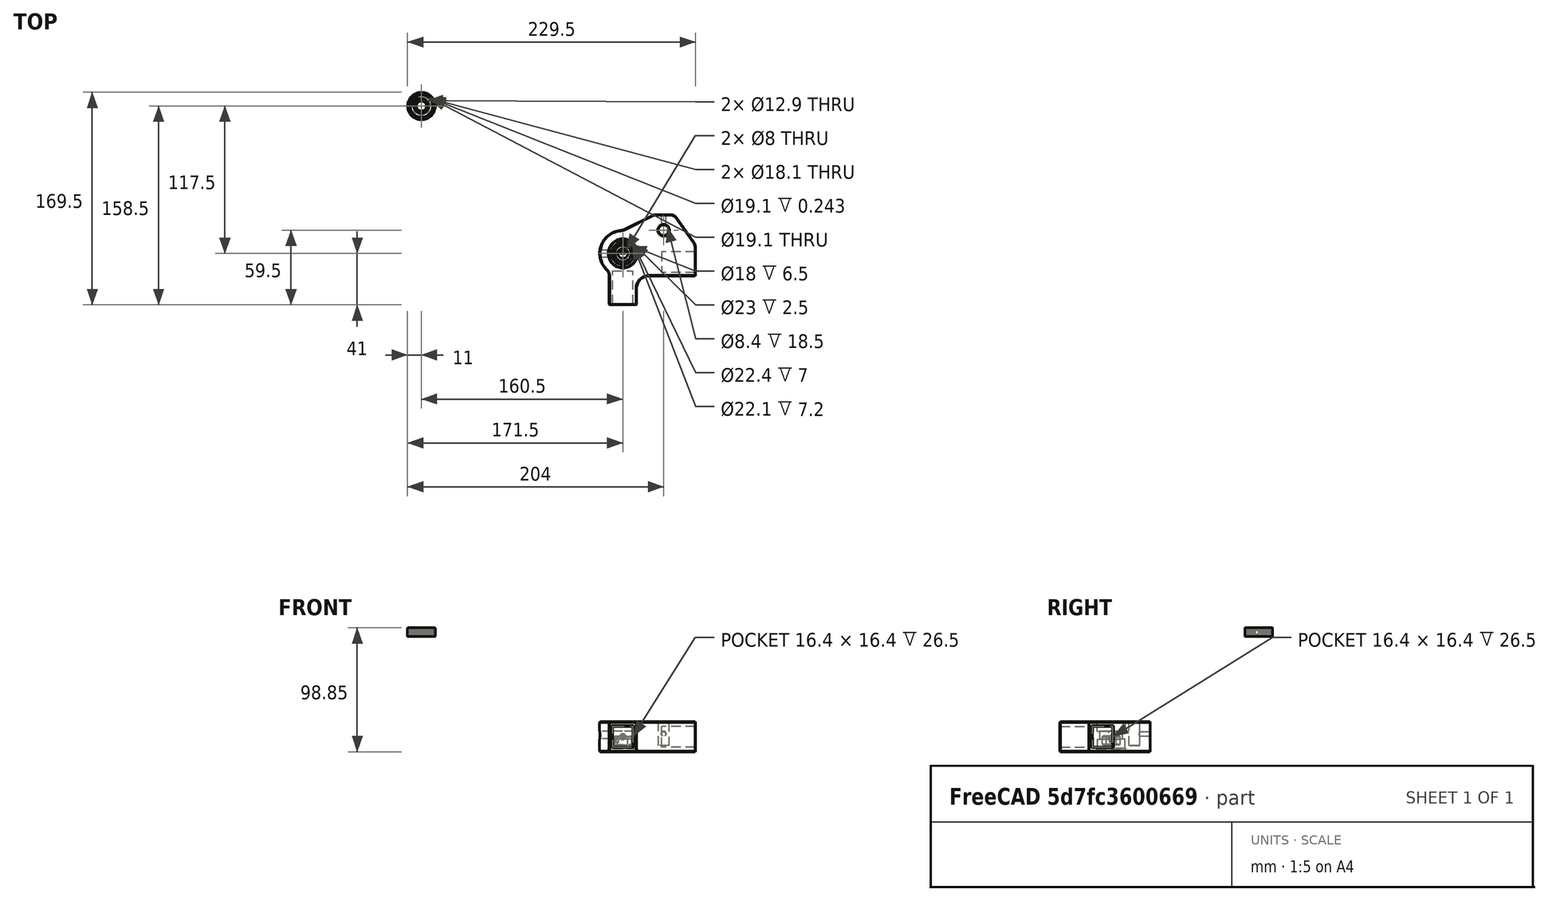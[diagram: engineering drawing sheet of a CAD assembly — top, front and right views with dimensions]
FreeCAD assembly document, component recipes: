
FREECAD ASSEMBLY — COMPONENT RECIPES ("MotorizedBed")

This assembly document has 4 components, labeled P0..P3 below (a component is one placed body or linked part). 1 of them carries a construction recipe — the FreeCAD feature program that regenerates the part from scratch, quoted from this document or its linked companion documents; the rest are supplied as boundary geometry only. No exploded tour is included for this assembly.
COMPONENT P0 — geometry summary ("VerrouillageVisTrapézoidale"; no construction recipe available for this part):
  bounding box: 14.2 x 14.0 x 7.0 mm
  tessellated surface: 100 triangles
  volume: 714 mm^3 (51% of its bounding box)
  symmetry: mirror-symmetric across its z mid-plane
COMPONENT P1 — recipe-attached ("LowerBracketTL", modeled in this document).
Construction recipe (the document's own serialized feature program — sketch geometry with constraints, then the solid features built on it; lengths are millimeters unless a unit is written):

FEATURE [Sketcher::SketchObject] Sketch
  ArcFitTolerance = 1e-06
  FullyConstrained = true
  MapMode = 5
  TreeRank = 141
  sketch-geometry (10):
    g0: LineSegment StartX=-11 StartY=-14.8745 StartZ=0 EndX=-11 EndY=-41 EndZ=0
    g1: LineSegment StartX=-11 StartY=-41 StartZ=0 EndX=11 EndY=-41 EndZ=0
    g2: LineSegment StartX=11 StartY=-41 StartZ=0 EndX=11 EndY=-18 EndZ=0
    g3: LineSegment StartX=11 StartY=-18 StartZ=0 EndX=58 EndY=-18 EndZ=0
    g4: LineSegment StartX=58 StartY=-18 StartZ=0 EndX=58 EndY=7 EndZ=0
    g5: LineSegment StartX=58 StartY=7 StartZ=0 EndX=41 EndY=31 EndZ=0
    g6: LineSegment StartX=41 StartY=31 StartZ=0 EndX=25 EndY=31 EndZ=0
    g7: Circle [constr] CenterX=0 CenterY=0 CenterZ=0 NormalX=0 NormalY=0 NormalZ=1 AngleXU=0 Radius=18.5
    g8: ArcOfCircle CenterX=0 CenterY=0 CenterZ=0 NormalX=0 NormalY=0 NormalZ=1 AngleXU=0 Radius=18.5 StartAngle=1.5708 EndAngle=4.07563
    g9: LineSegment StartX=0 StartY=18.5 StartZ=0 EndX=25 EndY=31 EndZ=0
  constraints (28):
    c: Vertical(g0)
    c: Coincident(g0,g1)
    c: Coincident(g1,g2)
    c: Vertical(g2)
    c: Coincident(g2,g3)
    c: Horizontal(g3)
    c: Coincident(g3,g4)
    c: Vertical(g4)
    c: Coincident(g4,g5)
    c: Coincident(g5,g6)
    c: Horizontal(g6)
    c: DistanceY(g0,g-1) = 41
    c: DistanceX(g0,g-1) = 11
    c: Symmetric(g0,g1,g-2)
    c: DistanceY(g3,g-1) = 18
    c: DistanceY(g-1,g4) = 7
    c: DistanceX(g-1,g6) = 25
    c: DistanceX(g-1,g5) = 41
    c: DistanceX(g-1,g3) = 58
    c: Coincident(g7,g-1)
    c: Diameter(g7) = 37
    c: Coincident(g8,g7)
    c: Coincident(g8,g0)
    c: PointOnObject(g8,g7)
    c: PointOnObject(g8,g-2)
    c: Coincident(g9,g8)
    c: Coincident(g9,g6)
    c: DistanceY(g8,g6) = 31
FEATURE [PartDesign::Pad] Pad  label="MainForm"
  AddSubType = 0
  AlongSketchNormal = false
  CheckUpToFaceLimits = true
  ClaimChildren = false
  Direction = (0,0,1)
  Fit = 0
  FitJoin = 0
  InnerFit = 0
  InnerFitJoin = 0
  InnerTaperAngle = 0
  InnerTaperAngleRev = 0
  Length = 24
  Length2 = 100
  Linearize = true
  Midplane = true
  NewSolid = false
  Profile = -> Sketch
  Suppress = false
  TreeRank = 29
  Type = 0
  _ProfileBasedVersion = 1
FEATURE [PartDesign::Fillet] Fillet
  AddSubType = 0
  Base = -> Pad [Edge8]
  BaseFeature = -> Pad
  NewSolid = false
  Radius = 10
  SupportTransform = false
  Suppress = false
  TreeRank = 30
FEATURE [PartDesign::Fillet] Fillet001
  AddSubType = 0
  Base = -> Fillet [Edge26]
  BaseFeature = -> Fillet
  NewSolid = false
  Radius = 6
  SupportTransform = false
  Suppress = false
  TreeRank = 31
FEATURE [PartDesign::Fillet] Fillet002
  AddSubType = 0
  Base = -> Fillet001 [Edge19]
  BaseFeature = -> Fillet001
  NewSolid = false
  Radius = 12
  SupportTransform = false
  Suppress = false
  TreeRank = 32
FEATURE [PartDesign::Fillet] Fillet003
  AddSubType = 0
  Base = -> Fillet002 [Edge20]
  BaseFeature = -> Fillet002
  NewSolid = false
  Radius = 7
  SupportTransform = false
  Suppress = false
  TreeRank = 33
FEATURE [PartDesign::Fillet] Fillet004
  AddSubType = 0
  Base = -> Fillet003 [Edge21]
  BaseFeature = -> Fillet003
  NewSolid = false
  Radius = 6
  SupportTransform = false
  Suppress = false
  TreeRank = 34
FEATURE [PartDesign::Fillet] Fillet005
  AddSubType = 0
  Base = -> Fillet004 [Edge22]
  BaseFeature = -> Fillet004
  NewSolid = false
  Radius = 9
  SupportTransform = false
  Suppress = false
  TreeRank = 35
FEATURE [Sketcher::SketchObject] Sketch001
  ArcFitTolerance = 1e-06
  AttachmentSupport = -> [Fillet005]
  FullyConstrained = true
  MapMode = 5
  Placement = pos=(0,-41,0) rot=(1,0,0;1.5708rad)
  Support = -> [Fillet005]
  TreeRank = 142
  sketch-geometry (4):
    g0: LineSegment StartX=-8.2 StartY=8.2 StartZ=0 EndX=8.2 EndY=8.2 EndZ=0
    g1: LineSegment StartX=8.2 StartY=8.2 StartZ=0 EndX=8.2 EndY=-8.2 EndZ=0
    g2: LineSegment StartX=8.2 StartY=-8.2 StartZ=0 EndX=-8.2 EndY=-8.2 EndZ=0
    g3: LineSegment StartX=-8.2 StartY=-8.2 StartZ=0 EndX=-8.2 EndY=8.2 EndZ=0
  constraints (11):
    c: Coincident(g0,g1)
    c: Coincident(g1,g2)
    c: Coincident(g2,g3)
    c: Coincident(g3,g0)
    c: Horizontal(g0)
    c: Horizontal(g2)
    c: Vertical(g1)
    c: Vertical(g3)
    c: Symmetric(g0,g2,g-1)
    c: Equal(g1,g0)
    c: DistanceX(g0,g0) = 16.4
FEATURE [PartDesign::Pocket] Pocket  label="CavitéProfilé"
  AddSubType = 1
  BaseFeature = -> Fillet005
  CheckUpToFaceLimits = true
  ClaimChildren = false
  Fit = 0
  FitJoin = 0
  InnerFit = 0
  InnerFitJoin = 0
  InnerTaperAngle = 0
  InnerTaperAngleRev = 0
  Length = 27
  Length2 = 100
  Linearize = true
  NewSolid = false
  Profile = -> Sketch001
  Suppress = false
  TreeRank = 37
  Type = 0
  _ProfileBasedVersion = 1
  _Version = 1
FEATURE [Sketcher::SketchObject] Sketch002
  ArcFitTolerance = 1e-06
  AttachmentSupport = -> [Pocket]
  ExternalGeometry = -> [Pocket]
  FullyConstrained = true
  MapMode = 5
  Placement = pos=(58,0,0) rot=(0.57735,0.57735,0.57735;2.0944rad)
  Support = -> [Pocket]
  TreeRank = 143
  sketch-geometry (6):
    g0: LineSegment StartX=-15.1323 StartY=8.2 StartZ=0 EndX=1.26771 EndY=8.2 EndZ=0
    g1: LineSegment StartX=1.26771 StartY=8.2 StartZ=0 EndX=1.26771 EndY=-8.2 EndZ=0
    g2: LineSegment StartX=1.26771 StartY=-8.2 StartZ=0 EndX=-15.1323 EndY=-8.2 EndZ=0
    g3: LineSegment StartX=-15.1323 StartY=-8.2 StartZ=0 EndX=-15.1323 EndY=8.2 EndZ=0
    g4: LineSegment [constr] StartX=-18 StartY=12 StartZ=0 EndX=4.13542 EndY=-12 EndZ=0
    g5: GeomPoint [constr] X=-6.93229 Y=0 Z=0
  constraints (15):
    c: Coincident(g0,g1)
    c: Coincident(g1,g2)
    c: Coincident(g2,g3)
    c: Coincident(g3,g0)
    c: Horizontal(g0)
    c: Horizontal(g2)
    c: Vertical(g1)
    c: Vertical(g3)
    c: DistanceX(g0,g0) = 16.4
    c: Coincident(g4,g-3)
    c: Coincident(g4,g-4)
    c: PointOnObject(g5,g4)
    c: PointOnObject(g5,g-1)
    c: Symmetric(g0,g1,g5)
    c: Equal(g0,g1)
FEATURE [PartDesign::Pocket] Pocket001  label="CavitéProfilé2"
  AddSubType = 1
  BaseFeature = -> Pocket
  CheckUpToFaceLimits = true
  ClaimChildren = false
  Fit = 0
  FitJoin = 0
  InnerFit = 0
  InnerFitJoin = 0
  InnerTaperAngle = 0
  InnerTaperAngleRev = 0
  Length = 27
  Length2 = 100
  Linearize = true
  NewSolid = false
  Profile = -> Sketch002
  Suppress = false
  TreeRank = 39
  Type = 0
  _ProfileBasedVersion = 1
  _Version = 1
FEATURE [PartDesign::Chamfer] Chamfer
  AddSubType = 0
  Angle = 45
  Base = -> Pocket001 [Edge45,Edge48,Edge47,Edge46,Edge28,Edge25,Edge26,Edge27]
  BaseFeature = -> Pocket001
  ChamferType = 0
  FlipDirection = false
  NewSolid = false
  Size = 0.5
  Size2 = 1
  SupportTransform = false
  Suppress = false
  TreeRank = 40
FEATURE [Sketcher::SketchObject] Sketch003
  ArcFitTolerance = 1e-06
  AttachmentSupport = -> [Chamfer]
  FullyConstrained = true
  MapMode = 5
  Placement = pos=(0,0,12) rot=(0,0,1;0rad)
  Support = -> [Chamfer]
  TreeRank = 144
  sketch-geometry (1):
    g0: Circle CenterX=0 CenterY=0 CenterZ=0 NormalX=0 NormalY=0 NormalZ=1 AngleXU=0 Radius=11.2
  constraints (2):
    c: Coincident(g0,g-1)
    c: Diameter(g0) = 22.4
FEATURE [PartDesign::Pocket] Pocket002  label="EmplacementRoulementSup"
  AddSubType = 1
  BaseFeature = -> Chamfer
  CheckUpToFaceLimits = true
  ClaimChildren = false
  Fit = 0
  FitJoin = 0
  InnerFit = 0
  InnerFitJoin = 0
  InnerTaperAngle = 0
  InnerTaperAngleRev = 0
  Length = 7.5
  Length2 = 100
  Linearize = true
  NewSolid = false
  Profile = -> Sketch003
  Suppress = false
  TreeRank = 42
  Type = 0
  _ProfileBasedVersion = 1
  _Version = 1
FEATURE [Sketcher::SketchObject] Sketch004
  ArcFitTolerance = 1e-06
  AttachmentSupport = -> [Pocket002]
  FullyConstrained = true
  MapMode = 5
  Placement = pos=(0,0,4.5) rot=(0,0,1;0rad)
  Support = -> [Pocket002]
  TreeRank = 145
  sketch-geometry (1):
    g0: Circle CenterX=0 CenterY=0 CenterZ=0 NormalX=0 NormalY=0 NormalZ=1 AngleXU=0 Radius=9
  constraints (2):
    c: Coincident(g0,g-1)
    c: Diameter(g0) = 18
FEATURE [PartDesign::Pocket] Pocket003  label="EmplacementBride"
  AddSubType = 1
  BaseFeature = -> Pocket002
  CheckUpToFaceLimits = true
  ClaimChildren = false
  Fit = 0
  FitJoin = 0
  InnerFit = 0
  InnerFitJoin = 0
  InnerTaperAngle = 0
  InnerTaperAngleRev = 0
  Length = 6.5
  Length2 = 100
  Linearize = true
  NewSolid = false
  Profile = -> Sketch004
  Suppress = false
  TreeRank = 44
  Type = 0
  _ProfileBasedVersion = 1
  _Version = 1
FEATURE [Sketcher::SketchObject] Sketch005
  ArcFitTolerance = 1e-06
  AttachmentSupport = -> [Pocket003]
  FullyConstrained = true
  MapMode = 5
  Placement = pos=(0,0,-2) rot=(0,0,1;0rad)
  Support = -> [Pocket003]
  TreeRank = 146
  sketch-geometry (1):
    g0: Circle CenterX=0 CenterY=0 CenterZ=0 NormalX=0 NormalY=0 NormalZ=1 AngleXU=0 Radius=11.05
  constraints (2):
    c: Coincident(g0,g-1)
    c: Diameter(g0) = 22.1
FEATURE [PartDesign::Pocket] Pocket004  label="EmplacementRoulementInf"
  AddSubType = 1
  BaseFeature = -> Pocket003
  CheckUpToFaceLimits = true
  ClaimChildren = false
  Fit = 0
  FitJoin = 0
  InnerFit = 0
  InnerFitJoin = 0
  InnerTaperAngle = 0
  InnerTaperAngleRev = 0
  Length = 7.5
  Length2 = 100
  Linearize = true
  NewSolid = false
  Profile = -> Sketch005
  Suppress = false
  TreeRank = 46
  Type = 0
  _ProfileBasedVersion = 1
  _Version = 1
FEATURE [Sketcher::SketchObject] Sketch006
  ArcFitTolerance = 1e-06
  AttachmentSupport = -> [Pocket004]
  FullyConstrained = true
  MapMode = 5
  Placement = pos=(0,0,-9.5) rot=(0,0,1;0rad)
  Support = -> [Pocket004]
  TreeRank = 147
  sketch-geometry (1):
    g0: Circle CenterX=0 CenterY=0 CenterZ=0 NormalX=0 NormalY=0 NormalZ=1 AngleXU=0 Radius=11.5
  constraints (2):
    c: Coincident(g0,g-1)
    c: Diameter(g0) = 23
FEATURE [PartDesign::Pocket] Pocket005
  AddSubType = 1
  BaseFeature = -> Pocket004
  CheckUpToFaceLimits = true
  ClaimChildren = false
  Fit = 0
  FitJoin = 0
  InnerFit = 0
  InnerFitJoin = 0
  InnerTaperAngle = 0
  InnerTaperAngleRev = 0
  Length = 5
  Length2 = 100
  Linearize = true
  NewSolid = false
  Profile = -> Sketch006
  Suppress = false
  TreeRank = 48
  Type = 1
  _ProfileBasedVersion = 1
  _Version = 1
FEATURE [PartDesign::Chamfer] Chamfer001
  AddSubType = 0
  Angle = 45
  Base = -> Pocket005 [Edge84]
  BaseFeature = -> Pocket005
  ChamferType = 0
  FlipDirection = false
  NewSolid = false
  Size = 0.3
  Size2 = 1
  SupportTransform = false
  Suppress = false
  TreeRank = 49
FEATURE [PartDesign::Chamfer] Chamfer002
  AddSubType = 0
  Angle = 45
  Base = -> Chamfer001 [Edge65]
  BaseFeature = -> Chamfer001
  ChamferType = 0
  FlipDirection = false
  NewSolid = false
  Size = 0.5
  Size2 = 1
  SupportTransform = false
  Suppress = false
  TreeRank = 50
FEATURE [PartDesign::Plane] DatumPlane  label="PlanAccesVis"
  AttachmentOffset = pos=(0,0,-19) rot=(0,0,1;0rad)
  AttachmentSupport = -> [YZ_Plane]
  Length = 10
  MapMode = 5
  MinimumLength = 10
  MinimumWidth = 10
  Placement = pos=(-19,4.2e-15,-4.2e-15) rot=(0.57735,0.57735,0.57735;2.0944rad)
  ResizeMode = 0
  Support = -> [YZ_Plane]
  TreeRank = 51
  Width = 10
FEATURE [Sketcher::SketchObject] Sketch007
  ArcFitTolerance = 1e-06
  AttachmentSupport = -> [DatumPlane]
  ExternalGeometry = -> [Chamfer002]
  FullyConstrained = true
  MapMode = 5
  Placement = pos=(-19,4.2e-15,-4.2e-15) rot=(0.57735,0.57735,0.57735;2.0944rad)
  Support = -> [DatumPlane]
  TreeRank = 148
  sketch-geometry (2):
    g0: Circle CenterX=0 CenterY=1.25 CenterZ=0 NormalX=0 NormalY=0 NormalZ=1 AngleXU=0 Radius=3
    g1: LineSegment [constr] StartX=9 StartY=4.5 StartZ=0 EndX=-9 EndY=-2 EndZ=0
  constraints (5):
    c: PointOnObject(g0,g-2)
    c: Coincident(g1,g-3)
    c: Coincident(g1,g-4)
    c: PointOnObject(g0,g1)
    c: Diameter(g0) = 6
FEATURE [PartDesign::Pocket] Pocket006  label="AccèsVis"
  AddSubType = 1
  BaseFeature = -> Chamfer002
  CheckUpToFaceLimits = true
  ClaimChildren = false
  Fit = 0
  FitJoin = 0
  InnerFit = 0
  InnerFitJoin = 0
  InnerTaperAngle = 0
  InnerTaperAngleRev = 0
  Length = 0
  Length2 = 100
  Linearize = true
  NewSolid = false
  Profile = -> Sketch007
  Suppress = false
  TreeRank = 53
  Type = 3
  UpToFace = -> Chamfer002 [Face38]
  _ProfileBasedVersion = 1
  _Version = 1
FEATURE [Sketcher::SketchObject] Sketch008
  ArcFitTolerance = 1e-06
  AttachmentSupport = -> [Pocket006]
  FullyConstrained = true
  MapMode = 5
  Placement = pos=(0,0,12) rot=(0,0,1;0rad)
  Support = -> [Pocket006]
  TreeRank = 149
  sketch-geometry (1):
    g0: Circle CenterX=32.5 CenterY=18.5 CenterZ=0 NormalX=0 NormalY=0 NormalZ=1 AngleXU=0 Radius=4.2
  constraints (3):
    c: DistanceY(g-1,g0) = 18.5
    c: DistanceX(g-1,g0) = 32.5
    c: Diameter(g0) = 8.4
FEATURE [PartDesign::Chamfer] Chamfer005
  AddSubType = 0
  Angle = 45
  Base = -> Pocket006 [Edge61]
  BaseFeature = -> Pocket006
  ChamferType = 0
  FlipDirection = false
  NewSolid = false
  Size = 0.5
  Size2 = 1
  SupportTransform = false
  Suppress = true
  TreeRank = 65
FEATURE [PartDesign::Chamfer] Chamfer006
  AddSubType = 0
  Angle = 45
  Base = -> Chamfer005 [Edge10,Edge7,Edge13,Edge40,Edge34,Edge51,Edge50,Edge43,Edge31]
  BaseFeature = -> Chamfer005
  ChamferType = 0
  FlipDirection = false
  NewSolid = false
  Size = 0.5
  Size2 = 1
  SupportTransform = false
  Suppress = false
  TreeRank = 63
FEATURE [PartDesign::Pocket] Pocket007  label="CavitéBarreLisse"
  AddSubType = 1
  BaseFeature = -> Chamfer006
  CheckUpToFaceLimits = true
  ClaimChildren = false
  Fit = 0
  FitJoin = 0
  InnerFit = 0
  InnerFitJoin = 0
  InnerTaperAngle = 0
  InnerTaperAngleRev = 0
  Length = 19
  Length2 = 100
  Linearize = true
  NewSolid = false
  Profile = -> Sketch008
  Suppress = false
  TreeRank = 55
  Type = 0
  _ProfileBasedVersion = 1
  _Version = 1
FEATURE [PartDesign::Chamfer] Chamfer003
  AddSubType = 0
  Angle = 45
  Base = -> Pocket007 [Edge17]
  BaseFeature = -> Pocket007
  ChamferType = 0
  FlipDirection = false
  NewSolid = false
  Size = 0.5
  Size2 = 1
  SupportTransform = false
  Suppress = false
  TreeRank = 56
FEATURE [Sketcher::SketchObject] Sketch009
  ArcFitTolerance = 1e-06
  AttachmentSupport = -> [Chamfer003]
  ExternalGeometry = -> [Chamfer003]
  FullyConstrained = true
  MapMode = 5
  Placement = pos=(0,31,0) rot=(0,0.707107,0.707107;3.14159rad)
  Support = -> [Chamfer003]
  TreeRank = 150
  sketch-geometry (3):
    g0: LineSegment [constr] StartX=-36.7 StartY=11.5 StartZ=0 EndX=-28.3 EndY=-7 EndZ=0
    g1: LineSegment [constr] StartX=-28.3 StartY=11.5 StartZ=0 EndX=-36.7 EndY=-7 EndZ=0
    g2: Circle CenterX=-32.5 CenterY=2.25 CenterZ=0 NormalX=0 NormalY=0 NormalZ=1 AngleXU=0 Radius=1.8
  constraints (7):
    c: Coincident(g0,g-4)
    c: Coincident(g0,g-3)
    c: Coincident(g1,g-4)
    c: Coincident(g1,g-3)
    c: PointOnObject(g2,g1)
    c: PointOnObject(g2,g0)
    c: Diameter(g2) = 3.6
FEATURE [PartDesign::Pocket] Pocket008  label="TrouVisFixationBarreLisse"
  AddSubType = 1
  BaseFeature = -> Chamfer003
  CheckUpToFaceLimits = true
  ClaimChildren = false
  Fit = 0
  FitJoin = 0
  InnerFit = 0
  InnerFitJoin = 0
  InnerTaperAngle = 0
  InnerTaperAngleRev = 0
  Length = 0
  Length2 = 100
  Linearize = true
  NewSolid = false
  Profile = -> Sketch009
  Suppress = false
  TreeRank = 58
  Type = 3
  UpToFace = -> Chamfer003 [Face19]
  _ProfileBasedVersion = 1
  _Version = 1
FEATURE [PartDesign::Chamfer] Chamfer004
  AddSubType = 0
  Angle = 45
  Base = -> Pocket008 [Edge100]
  BaseFeature = -> Pocket008
  ChamferType = 0
  FlipDirection = false
  NewSolid = false
  Size = 0.3
  Size2 = 1
  SupportTransform = false
  Suppress = false
  TreeRank = 64
FEATURE [PartDesign::Chamfer] Chamfer007
  AddSubType = 0
  Angle = 45
  Base = -> Chamfer004 [Edge139]
  BaseFeature = -> Chamfer004
  ChamferType = 0
  FlipDirection = false
  NewSolid = false
  Size = 0.5
  Size2 = 1
  SupportTransform = false
  Suppress = false
  TreeRank = 66
FEATURE [PartDesign::Body] Body  label="BasePlastique"
  AutoGroupSolids = false
  ClaimAllChildren = false
  ExportMode = 0
  Group = -> [Sketch,Pad,Fillet,Fillet001,Fillet002,Fillet003,Fillet004,Fillet005,Sketch001,Pocket,Sketch002,Pocket001,Chamfer,Sketch003,Pocket002,Sketch004,Pocket003,Sketch005,Pocket004,Sketch006,Pocket005,Chamfer001,Chamfer002,DatumPlane,Sketch007,Pocket006,Sketch008,Chamfer005,Chamfer006,Pocket007,Chamfer003,Sketch009,Pocket008,Chamfer004,Chamfer007]
  Origin = -> Origin001
  Tip = -> Chamfer007
  TreeRank = 14
  _ExportChildren = -> [Pad,Fillet,Fillet001,Fillet002,Fillet003,Fillet004,Fillet005,Pocket,Pocket001,Chamfer,Pocket002,Pocket003,Pocket004,Pocket005,Chamfer001,Chamfer002,DatumPlane,Pocket006,Chamfer005,Chamfer006,Pocket007,Chamfer003,Pocket008,Chamfer004,Chamfer007]
  _GroupVersion = 1
COMPONENT P2 — geometry summary ("Roulement608ZZ"; no construction recipe available for this part):
  bounding box: 22.0 x 22.0 x 7.0 mm
  tessellated surface: 9,142 triangles
  volume: 239452428260295137926477615583307857623072810892754607978231624669242043253247641482944024462204888315424909219004803609641569868769369479364049461313536 mm^3 (7067663171791474525991105169905080117868465916261901613621299298981183595544015703909911496714715540985324554045445061369218863302614646417627746926592% of its bounding box)
  symmetry: 2-fold rotationally symmetric about the y axis; mirror-symmetric across its x mid-plane, z mid-plane
COMPONENT P3 — geometry summary ("InsertM3"; no construction recipe available for this part):
  bounding box: 4.6 x 4.6 x 3.0 mm
  tessellated surface: 1,800 triangles
  volume: 119726214130147568963238807791653928811536405446377303989115812334621021626623820741472012231102444157712454609502401804820784934384684739682024730656768 mm^3 (188793067417424814426019444688636395670683878420661541013467033827670795419742562833852327770783847006854607819522394045061712498791544725597400204312576% of its bounding box)
PROVENANCE & LICENSES
A FreeCAD (.FCStd) document from a public repository crawl; recipes are the document's own serialized feature recipes (and, for linked parts, companion documents' recipes).
License: as declared in the source repository (recorded in the dataset sidecar).
